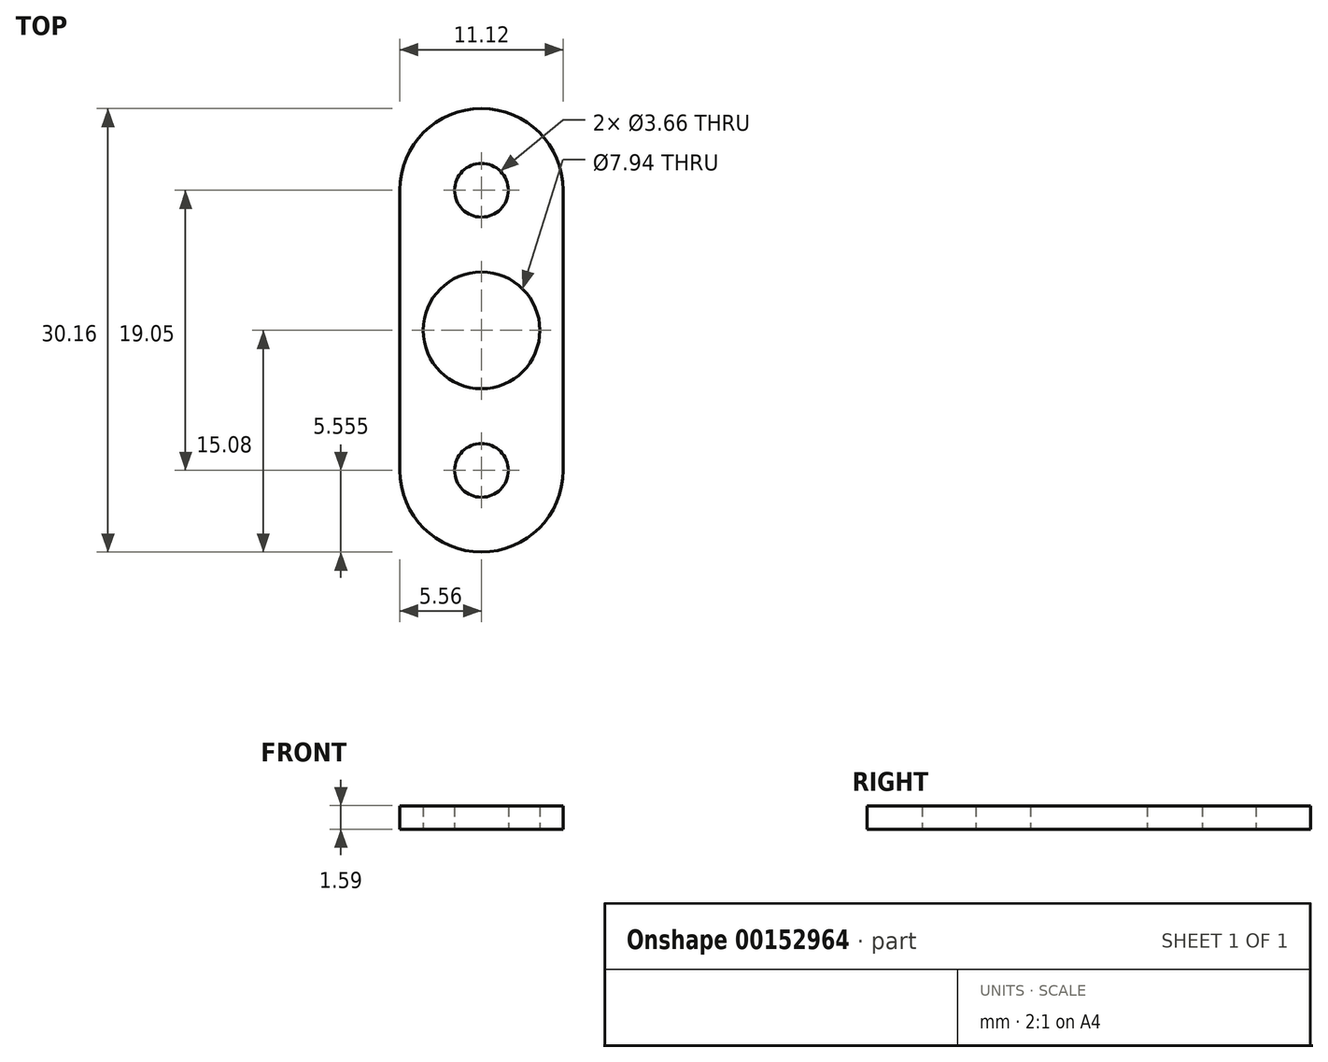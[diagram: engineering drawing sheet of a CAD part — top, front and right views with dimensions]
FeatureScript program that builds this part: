
annotation { "Feature Type Name" : "Feature", "Feature Type Description" : "" }
export const myFeature = defineFeature(function(context is Context, id is Id, definition is map)
    precondition{}
    {
        {
            var Q0;
            Q0=qCreatedBy(makeId("Top.planeOp"),FACE);
            var sketch = newSketch(context, id + "F0", { "sketchPlane" : qUnion([Q0])});
            skLineSegment(sketch, "E0.bottom", {"start": v(5.56, 9.53) * mm, "end": v(-5.56, 9.53) * mm, "construction": true});
            skLineSegment(sketch, "E0.top", {"start": v(5.56, -9.53) * mm, "end": v(-5.56, -9.53) * mm, "construction": true});
            skLineSegment(sketch, "E0.left", {"start": v(5.56, 9.53) * mm, "end": v(5.56, -9.53) * mm});
            skLineSegment(sketch, "E0.right", {"start": v(-5.56, 9.53) * mm, "end": v(-5.56, -9.53) * mm});
            skPoint(sketch, "E0.middle", {"position": v(0, 0) * mm});
            skArc(sketch, "E1", {"start": v(5.56, 9.53) * mm, "mid": v(0, 15.08) * mm, "end": v(-5.56, 9.53) * mm});
            skArc(sketch, "E2", {"start": v(-5.56, -9.52) * mm, "mid": v(0, -15.08) * mm, "end": v(5.56, -9.52) * mm});
            skCircle(sketch, "E3", {"center": v(0, 9.53) * mm, "radius": 1.83 * mm});
            skCircle(sketch, "E4", {"center": v(0, -9.52) * mm, "radius": 1.83 * mm});
            skCircle(sketch, "E5", {"center": v(0, 0) * mm, "radius": 3.97 * mm});
            skSolve(sketch);
        }
        {
            var Q0;
            Q0 = qSketchRegion(id + "F0", true);
            extrude(context, id + "F1", {"entities" : qUnion([Q0]), "depth" : 1.59 * mm});
        }
    });
